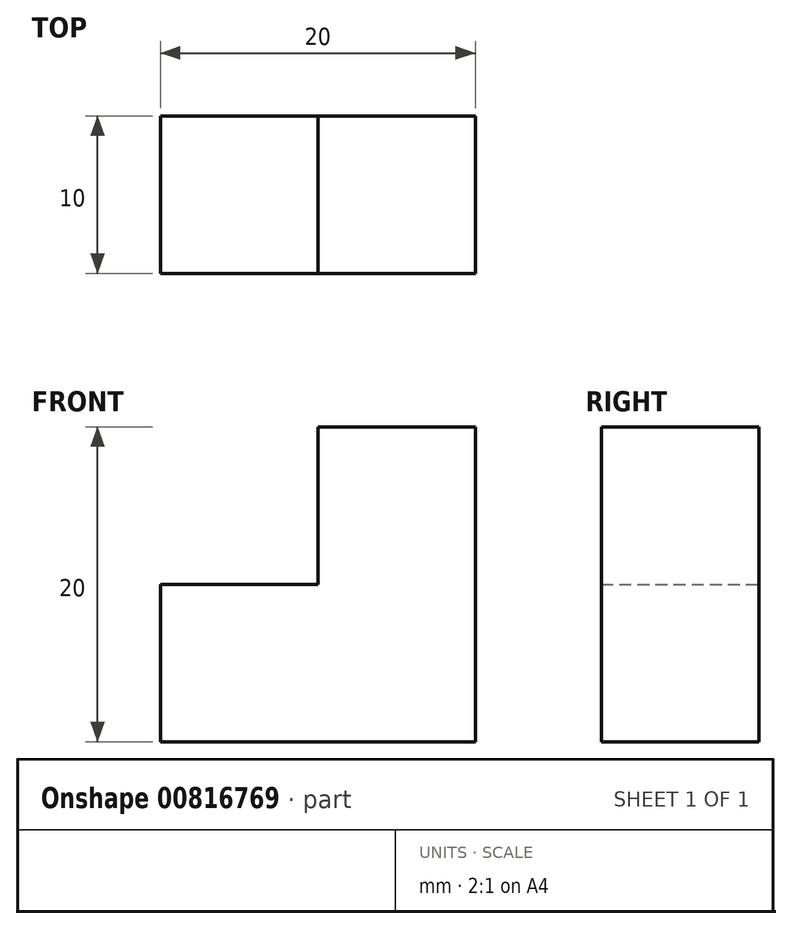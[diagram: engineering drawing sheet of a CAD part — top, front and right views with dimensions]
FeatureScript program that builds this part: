
annotation { "Feature Type Name" : "Feature", "Feature Type Description" : "" }
export const myFeature = defineFeature(function(context is Context, id is Id, definition is map)
    precondition{}
    {
        {
            var Q0;
            Q0=qCreatedBy(makeId("Top.planeOp"),FACE);
            var sketch = newSketch(context, id + "F0", { "sketchPlane" : qUnion([Q0])});
            skLineSegment(sketch, "E0.bottom", {"start": v(0, 0) * mm, "end": v(10, 0) * mm});
            skLineSegment(sketch, "E0.top", {"start": v(0, 10) * mm, "end": v(10, 10) * mm});
            skLineSegment(sketch, "E0.left", {"start": v(0, 0) * mm, "end": v(0, 10) * mm});
            skLineSegment(sketch, "E0.right", {"start": v(10, 0) * mm, "end": v(10, 10) * mm});
            skSolve(sketch);
        }
        {
            var Q0;
            Q0 = qSketchRegion(id + "F0", true);
            extrude(context, id + "F1", {"entities" : qUnion([Q0]), "depth" : 20 * mm, "offsetDistance" : 25 * mm});
        }
        {
            var Q0;
            Q0=makeQuery(id+"F1.opExtrude","SWEPT_FACE",FACE,{"disambiguationData":[OSD([sQuery(id+"F0.wireOp",EDGE,"E0.left")])]});
            var sketch = newSketch(context, id + "F2", { "sketchPlane" : qUnion([Q0])});
            skLineSegment(sketch, "E1.bottom", {"start": v(0, 0) * mm, "end": v(-10, 0) * mm});
            skLineSegment(sketch, "E1.top", {"start": v(0, 10) * mm, "end": v(-10, 10) * mm});
            skLineSegment(sketch, "E1.left", {"start": v(0, 0) * mm, "end": v(0, 10) * mm});
            skLineSegment(sketch, "E1.right", {"start": v(-10, 0) * mm, "end": v(-10, 10) * mm});
            skSolve(sketch);
        }
        {
            var Q0;
            Q0 = qSketchRegion(id + "F2", true);
            var Q1;
            Q1=makeQuery(id+"F2.imprint","IMPRINT",FACE,{"disambiguationData":[TD([[makeQuery(id+"F2.imprint","IMPRINT",EDGE,{"derivedFrom":sQuery(id+"F2.wireOp",EDGE,"E1.bottom")}),-1.0]])]});
            extrude(context, id + "F3", {"entities" : qUnion([Q0, Q1]), "operationType" : NewBodyOperationType.ADD, "depth" : 10 * mm, "offsetDistance" : 25 * mm});
        }
    });
